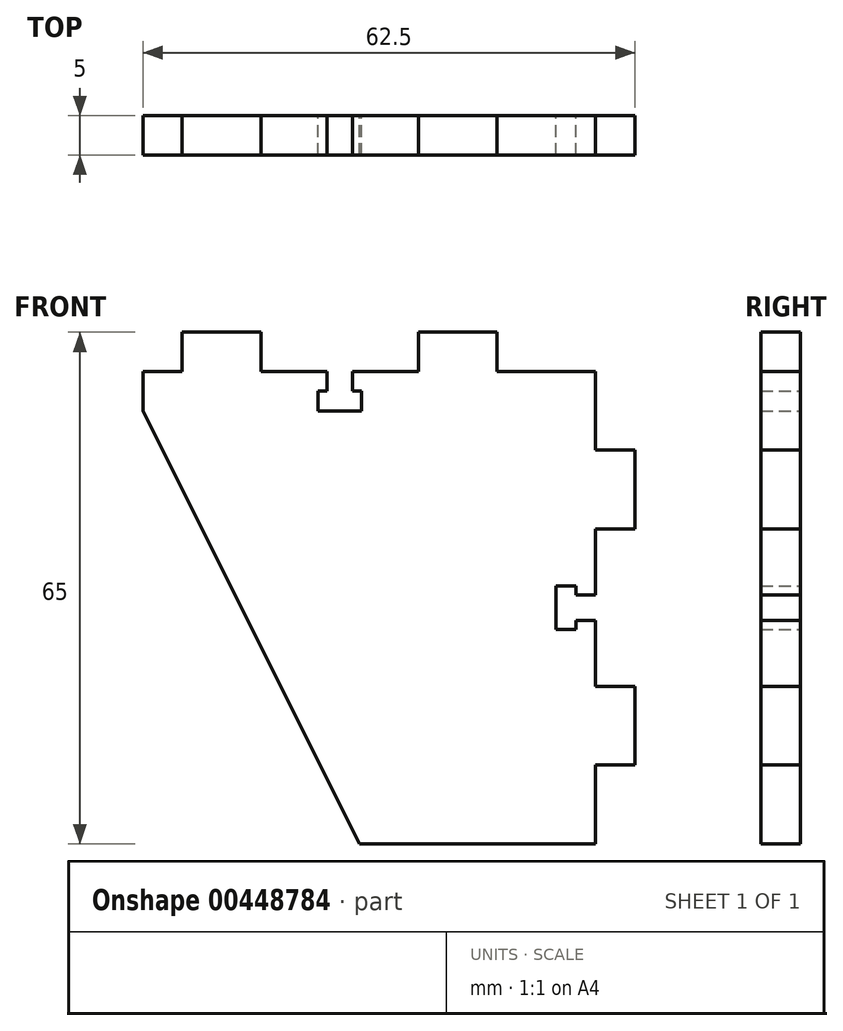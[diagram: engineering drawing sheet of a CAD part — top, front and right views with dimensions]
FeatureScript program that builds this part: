
annotation { "Feature Type Name" : "Feature", "Feature Type Description" : "" }
export const myFeature = defineFeature(function(context is Context, id is Id, definition is map)
    precondition{}
    {
        {
            assignVariable(context, id + "F0", {"name" : "thickness", "anyValue" : 5 * mm});
        }
        {
            var Q0;
            Q0=qCreatedBy(makeId("Front.planeOp"),FACE);
            var sketch = newSketch(context, id + "F1", { "sketchPlane" : qUnion([Q0])});
            skLineSegment(sketch, "E0", {"start": v(0, 0) * mm, "end": v(-30, 0) * mm});
            skLineSegment(sketch, "E1", {"start": v(-57.5, 60) * mm, "end": v(-52.5, 60) * mm});
            skLineSegment(sketch, "E2", {"start": v(0, 60) * mm, "end": v(0, 50) * mm});
            skPoint(sketch, "E3.centerSnap1", {"position": v(0, 30) * mm});
            skLineSegment(sketch, "E4", {"start": v(-52.5, 60) * mm, "end": v(-52.5, 65) * mm});
            skLineSegment(sketch, "E5", {"start": v(-52.5, 65) * mm, "end": v(-42.5, 65) * mm});
            skLineSegment(sketch, "E6", {"start": v(-42.5, 65) * mm, "end": v(-42.5, 60) * mm});
            skLineSegment(sketch, "E7", {"start": v(-22.5, 60) * mm, "end": v(-22.5, 65) * mm});
            skLineSegment(sketch, "E8", {"start": v(-22.5, 65) * mm, "end": v(-12.5, 65) * mm});
            skLineSegment(sketch, "E9", {"start": v(-12.5, 65) * mm, "end": v(-12.5, 60) * mm});
            skLineSegment(sketch, "E10", {"start": v(-34.1, 60) * mm, "end": v(-34.1, 57.5) * mm});
            skLineSegment(sketch, "E11", {"start": v(-34.1, 57.5) * mm, "end": v(-35.25, 57.5) * mm});
            skLineSegment(sketch, "E12", {"start": v(-35.25, 57.5) * mm, "end": v(-35.25, 55) * mm});
            skLineSegment(sketch, "E13", {"start": v(-35.25, 55) * mm, "end": v(-32.5, 55) * mm});
            skLineSegment(sketch, "E14", {"start": v(-32.5, 55) * mm, "end": v(-32.5, 60) * mm, "construction": true});
            skLineSegment(sketch, "E15.MirrorCS", {"start": v(-30.9, 57.5) * mm, "end": v(-29.75, 57.5) * mm});
            skLineSegment(sketch, "E16.MirrorCS", {"start": v(-29.75, 57.5) * mm, "end": v(-29.75, 55) * mm});
            skLineSegment(sketch, "E17.MirrorCS", {"start": v(-30.9, 60) * mm, "end": v(-30.9, 57.5) * mm});
            skLineSegment(sketch, "E18.MirrorCS", {"start": v(-29.75, 55) * mm, "end": v(-32.5, 55) * mm});
            skLineSegment(sketch, "E19.trimOffspring", {"start": v(-30.9, 60) * mm, "end": v(-22.5, 60) * mm});
            skLineSegment(sketch, "E20.trimOffspring", {"start": v(-42.5, 60) * mm, "end": v(-34.1, 60) * mm});
            skLineSegment(sketch, "E21.trimOffspring", {"start": v(-12.5, 60) * mm, "end": v(0, 60) * mm});
            skLineSegment(sketch, "E22", {"start": v(0, 50) * mm, "end": v(5, 50) * mm});
            skLineSegment(sketch, "E23", {"start": v(5, 50) * mm, "end": v(5, 40) * mm});
            skLineSegment(sketch, "E24", {"start": v(5, 40) * mm, "end": v(0, 40) * mm});
            skLineSegment(sketch, "E25", {"start": v(0, 20) * mm, "end": v(5, 20) * mm});
            skLineSegment(sketch, "E26", {"start": v(5, 20) * mm, "end": v(5, 10) * mm});
            skLineSegment(sketch, "E27", {"start": v(5, 10) * mm, "end": v(0, 10) * mm});
            skLineSegment(sketch, "E28", {"start": v(0, 31.6) * mm, "end": v(-2.5, 31.6) * mm});
            skLineSegment(sketch, "E29", {"start": v(-2.5, 31.6) * mm, "end": v(-2.5, 32.75) * mm});
            skLineSegment(sketch, "E30", {"start": v(-2.5, 32.75) * mm, "end": v(-5, 32.75) * mm});
            skLineSegment(sketch, "E31", {"start": v(-5, 32.75) * mm, "end": v(-5, 30) * mm});
            skLineSegment(sketch, "E32", {"start": v(-5, 30) * mm, "end": v(0, 30) * mm, "construction": true});
            skLineSegment(sketch, "E33.MirrorCS", {"start": v(-2.5, 28.4) * mm, "end": v(-2.5, 27.25) * mm});
            skLineSegment(sketch, "E34.MirrorCS", {"start": v(-2.5, 27.25) * mm, "end": v(-5, 27.25) * mm});
            skLineSegment(sketch, "E35.MirrorCS", {"start": v(0, 28.4) * mm, "end": v(-2.5, 28.4) * mm});
            skLineSegment(sketch, "E36.MirrorCS", {"start": v(-5, 27.25) * mm, "end": v(-5, 30) * mm});
            skLineSegment(sketch, "E37", {"start": v(0, 40) * mm, "end": v(0, 31.6) * mm, "construction": true});
            skLineSegment(sketch, "E38.trimOffspring", {"start": v(0, 40) * mm, "end": v(0, 31.6) * mm});
            skLineSegment(sketch, "E39.trimOffspring", {"start": v(0, 28.4) * mm, "end": v(0, 20) * mm, "construction": true});
            skLineSegment(sketch, "E40.trimOffspring", {"start": v(0, 28.4) * mm, "end": v(0, 20) * mm});
            skLineSegment(sketch, "E41.trimOffspring", {"start": v(0, 10) * mm, "end": v(0, 0) * mm});
            skLineSegment(sketch, "E42", {"start": v(-57.5, 60) * mm, "end": v(-57.5, 55) * mm});
            skLineSegment(sketch, "E43", {"start": v(-57.5, 55) * mm, "end": v(-30, 0) * mm});
            skSolve(sketch);
        }
        {
            var Q0;
            Q0=qSketchRegion(id+"F1",true);
            extrude(context, id + "F2", {"entities" : qUnion([Q0]), "depth" : getVariable(context, 'thickness')});
        }
    });
